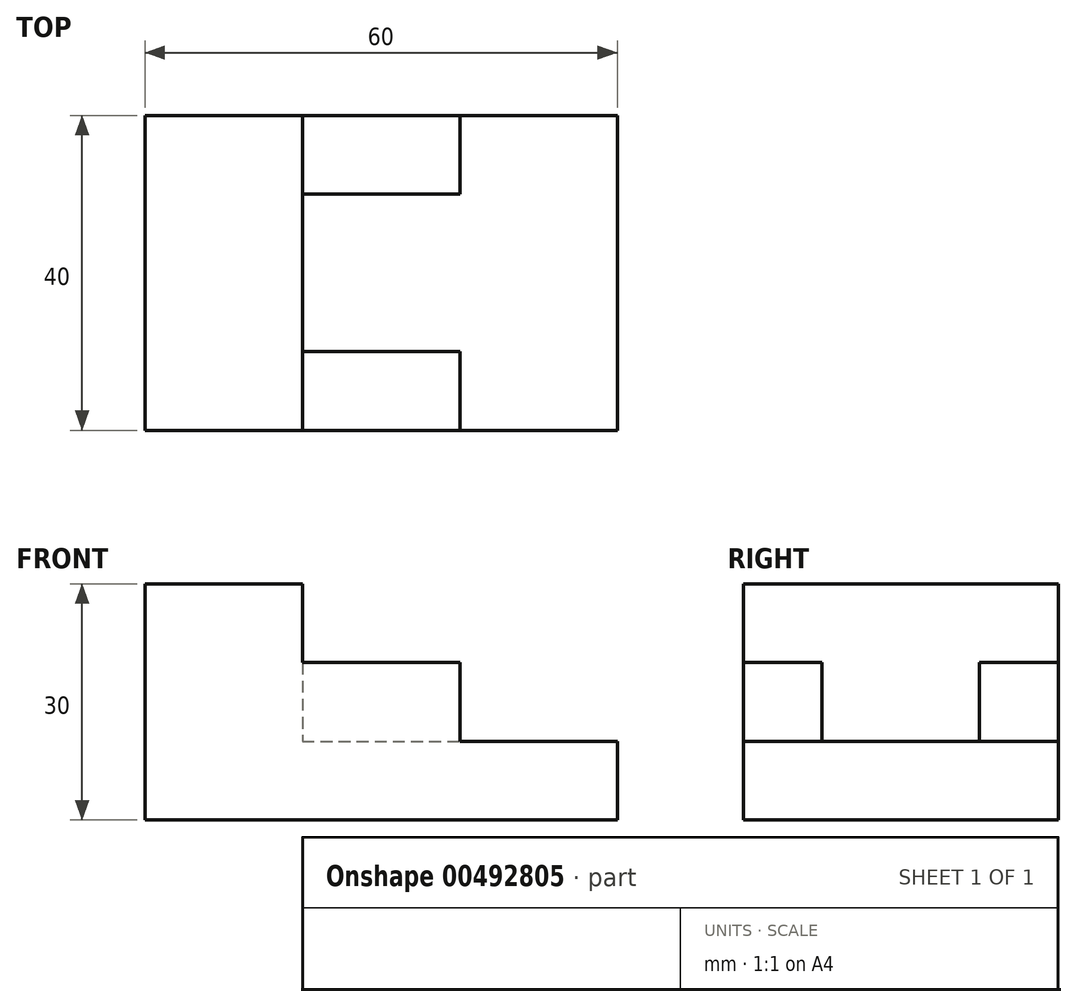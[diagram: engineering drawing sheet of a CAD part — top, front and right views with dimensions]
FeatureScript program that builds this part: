
annotation { "Feature Type Name" : "Feature", "Feature Type Description" : "" }
export const myFeature = defineFeature(function(context is Context, id is Id, definition is map)
    precondition{}
    {
        {
            var Q0;
            Q0=qCreatedBy(makeId("Top.planeOp"),FACE);
            var sketch = newSketch(context, id + "F0", { "sketchPlane" : qUnion([Q0])});
            skLineSegment(sketch, "E0.bottom", {"start": v(-30, 20) * mm, "end": v(30, 20) * mm});
            skLineSegment(sketch, "E0.top", {"start": v(-30, -20) * mm, "end": v(30, -20) * mm});
            skLineSegment(sketch, "E0.left", {"start": v(-30, 20) * mm, "end": v(-30, -20) * mm});
            skLineSegment(sketch, "E0.right", {"start": v(30, 20) * mm, "end": v(30, -20) * mm});
            skPoint(sketch, "E0.middle", {"position": v(0, 0) * mm});
            skSolve(sketch);
        }
        {
            var Q0;
            Q0 = qSketchRegion(id + "F0", true);
            extrude(context, id + "F1", {"entities" : qUnion([Q0]), "depth" : 10 * mm});
        }
        {
            var Q0;
            Q0=makeQuery(id+"F1.opExtrude","CAP_FACE",FACE,{"disambiguationData":[OSD([sQuery(id+"F0.wireOp",EDGE,"E0.bottom"),sQuery(id+"F0.wireOp",EDGE,"E0.top"),sQuery(id+"F0.wireOp",EDGE,"E0.left"),sQuery(id+"F0.wireOp",EDGE,"E0.right")])],"isStart":false});
            var sketch = newSketch(context, id + "F2", { "sketchPlane" : qUnion([Q0])});
            skLineSegment(sketch, "E1.bottom", {"start": v(-30, 20) * mm, "end": v(-10, 20) * mm});
            skLineSegment(sketch, "E1.top", {"start": v(-30, -20) * mm, "end": v(-10, -20) * mm});
            skLineSegment(sketch, "E1.left", {"start": v(-30, 20) * mm, "end": v(-30, -20) * mm});
            skLineSegment(sketch, "E1.right", {"start": v(-10, 20) * mm, "end": v(-10, -20) * mm});
            skSolve(sketch);
        }
        {
            var Q0;
            Q0 = qSketchRegion(id + "F2", true);
            extrude(context, id + "F3", {"entities" : qUnion([Q0]), "operationType" : NewBodyOperationType.ADD, "depth" : 20 * mm});
        }
        {
            var Q0;
            Q0=makeQuery(id+"F1.opExtrude","CAP_FACE",FACE,{"disambiguationData":[OSD([sQuery(id+"F0.wireOp",EDGE,"E0.bottom"),sQuery(id+"F0.wireOp",EDGE,"E0.top"),sQuery(id+"F0.wireOp",EDGE,"E0.left"),sQuery(id+"F0.wireOp",EDGE,"E0.right")])],"isStart":false});
            var sketch = newSketch(context, id + "F4", { "sketchPlane" : qUnion([Q0])});
            skLineSegment(sketch, "E2.bottom", {"start": v(-10, -20) * mm, "end": v(10, -20) * mm});
            skLineSegment(sketch, "E2.top", {"start": v(-10, -10) * mm, "end": v(10, -10) * mm});
            skLineSegment(sketch, "E2.left", {"start": v(-10, -20) * mm, "end": v(-10, -10) * mm});
            skLineSegment(sketch, "E2.right", {"start": v(10, -20) * mm, "end": v(10, -10) * mm});
            skSolve(sketch);
        }
        {
            var Q0;
            Q0 = qSketchRegion(id + "F4", true);
            extrude(context, id + "F5", {"entities" : qUnion([Q0]), "operationType" : NewBodyOperationType.ADD, "depth" : 10 * mm});
        }
        {
            var Q0;
            Q0=makeQuery(id+"F1.opExtrude","CAP_FACE",FACE,{"disambiguationData":[OSD([sQuery(id+"F0.wireOp",EDGE,"E0.bottom"),sQuery(id+"F0.wireOp",EDGE,"E0.top"),sQuery(id+"F0.wireOp",EDGE,"E0.left"),sQuery(id+"F0.wireOp",EDGE,"E0.right")])],"isStart":false});
            var sketch = newSketch(context, id + "F6", { "sketchPlane" : qUnion([Q0])});
            skLineSegment(sketch, "E3.bottom", {"start": v(-10, 20) * mm, "end": v(10, 20) * mm});
            skLineSegment(sketch, "E3.top", {"start": v(-10, 10) * mm, "end": v(10, 10) * mm});
            skLineSegment(sketch, "E3.left", {"start": v(-10, 20) * mm, "end": v(-10, 10) * mm});
            skLineSegment(sketch, "E3.right", {"start": v(10, 20) * mm, "end": v(10, 10) * mm});
            skSolve(sketch);
        }
        {
            var Q0;
            Q0 = qSketchRegion(id + "F6", true);
            extrude(context, id + "F7", {"entities" : qUnion([Q0]), "operationType" : NewBodyOperationType.ADD, "depth" : 10 * mm});
        }
    });
